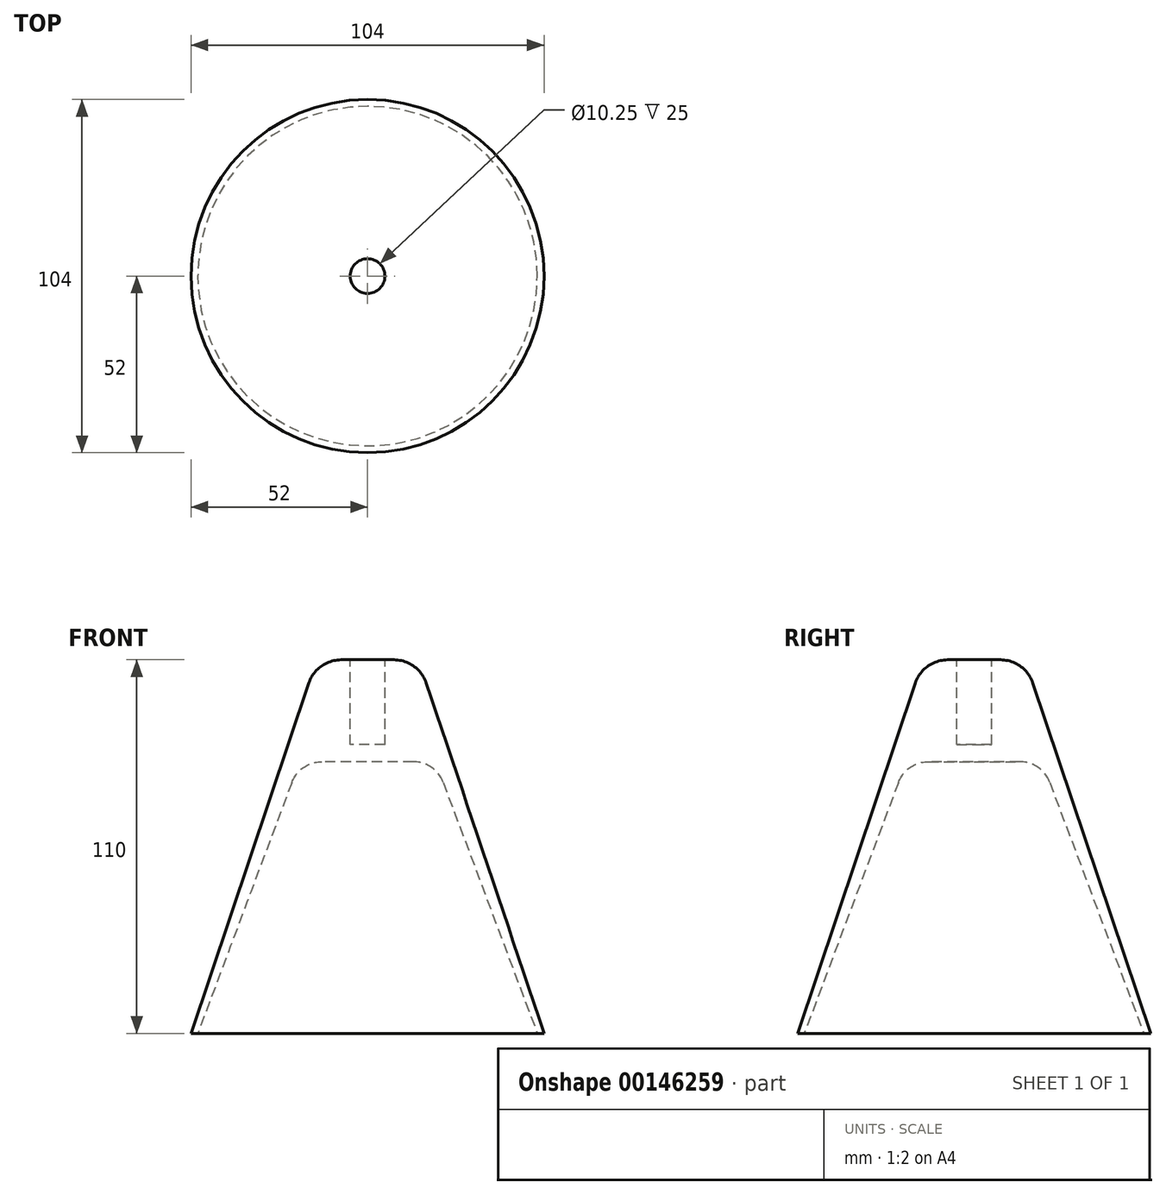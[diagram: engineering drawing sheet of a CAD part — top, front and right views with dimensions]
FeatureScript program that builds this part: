
annotation { "Feature Type Name" : "Feature", "Feature Type Description" : "" }
export const myFeature = defineFeature(function(context is Context, id is Id, definition is map)
    precondition{}
    {
        {
            var Q0;
            Q0=qCreatedBy(makeId("Top.planeOp"),FACE);
            var sketch = newSketch(context, id + "F0", { "sketchPlane" : qUnion([Q0])});
            skCircle(sketch, "E0", {"center": v(0, 0) * mm, "radius": 52 * mm});
            skSolve(sketch);
        }
        {
            var Q0;
            Q0=qCreatedBy(makeId("Top.planeOp"),FACE);
            cPlane(context, id + "F1", {"entities" : qUnion([Q0]), "cplaneType" : CPlaneType.OFFSET, "offset" : 80 * mm, "width" : 150 * mm, "height" : 150 * mm});
        }
        {
            var Q0;
            Q0=qCreatedBy(id+"F1.planeOp",FACE);
            var sketch = newSketch(context, id + "F2", { "sketchPlane" : qUnion([Q0])});
            skCircle(sketch, "E1", {"center": v(0, 0) * mm, "radius": 20 * mm});
            skSolve(sketch);
        }
        {
            var Q0;
            Q0=qCreatedBy(id+"F1.planeOp",FACE);
            cPlane(context, id + "F3", {"entities" : qUnion([Q0]), "cplaneType" : CPlaneType.OFFSET, "offset" : 30 * mm, "width" : 150 * mm, "height" : 150 * mm});
        }
        {
            var Q0;
            Q0=qCreatedBy(id+"F3.planeOp",FACE);
            var sketch = newSketch(context, id + "F4", { "sketchPlane" : qUnion([Q0])});
            skCircle(sketch, "E2", {"center": v(0, 0) * mm, "radius": 15 * mm});
            skSolve(sketch);
        }
        {
            var Q0;
            Q0=makeQuery(id+"F0.imprint","IMPRINT",FACE,{"disambiguationData":[TD([[makeQuery(id+"F0.imprint","IMPRINT",EDGE,{"derivedFrom":sQuery(id+"F0.wireOp",EDGE,"E0")}),1.0]])]});
            var Q1;
            Q1=makeQuery(id+"F4.imprint","IMPRINT",FACE,{"disambiguationData":[TD([[makeQuery(id+"F4.imprint","IMPRINT",EDGE,{"derivedFrom":sQuery(id+"F4.wireOp",EDGE,"E2")}),1.0]])]});
            loft(context, id + "F5", {"sheetProfilesArray" : [{ "sheetProfileEntities" : qUnion([Q0]) }, { "sheetProfileEntities" : qUnion([Q1]) }]});
        }
        {
            var Q0;
            Q0=makeQuery(id+"F5.opLoft","CAP_FACE",FACE,{"disambiguationData":[OSD([makeQuery(id+"F0.imprint","IMPRINT",FACE,{"disambiguationData":[TD([[makeQuery(id+"F0.imprint","IMPRINT",EDGE,{"derivedFrom":sQuery(id+"F0.wireOp",EDGE,"E0")}),1.0]])]})])],"isStart":true});
            var sketch = newSketch(context, id + "F6", { "sketchPlane" : qUnion([Q0])});
            skCircle(sketch, "E3", {"center": v(0, 0) * mm, "radius": 50 * mm});
            skSolve(sketch);
        }
        {
            var Q1;
            Q1 = qSketchRegion(id + "F2", true);
            var Q2;
            Q2 = qSketchRegion(id + "F6", true);
            loft(context, id + "F7", {"operationType" : NewBodyOperationType.REMOVE, "sheetProfilesArray" : [{ "sheetProfileEntities" : qUnion([Q1]) }, { "sheetProfileEntities" : qUnion([Q2]) }]});
        }
        {
            var Q0;
            Q0=makeQuery(id+"F5.opLoft","CAP_FACE",FACE,{"disambiguationData":[OSD([makeQuery(id+"F4.imprint","IMPRINT",FACE,{"disambiguationData":[TD([[makeQuery(id+"F4.imprint","IMPRINT",EDGE,{"derivedFrom":sQuery(id+"F4.wireOp",EDGE,"E2")}),1.0]])]})])],"isStart":true});
            var sketch = newSketch(context, id + "F8", { "sketchPlane" : qUnion([Q0])});
            skSolve(sketch);
        }
        {
            var Q0;
            Q0=makeQuery(id+"F8.imprint","IMPRINT",FACE,{"disambiguationData":[TD([[makeQuery(id+"F8.imprint","IMPRINT",EDGE,{"derivedFrom":makeQuery(id+"F5.opLoft","MID_CAP_EDGE",EDGE,{"disambiguationData":[OSD([sQuery(id+"F0.wireOp",EDGE,"E0"),sQuery(id+"F4.wireOp",EDGE,"E2")])],"capPos":1.0})}),1.0]])]});
            var sketch = newSketch(context, id + "F9", { "sketchPlane" : qUnion([Q0])});
            skCircle(sketch, "E4", {"center": v(0, 0) * mm, "radius": 5.12 * mm});
            skSolve(sketch);
        }
        {
            var Q0;
            Q0 = qSketchRegion(id + "F9", true);
            extrude(context, id + "F10", {"entities" : qUnion([Q0]), "operationType" : NewBodyOperationType.REMOVE, "oppositeDirection" : true, "depth" : 25 * mm});
        }
        {
            var Q0;
            Q0=makeQuery(id+"F5.opLoft","MID_CAP_EDGE",EDGE,{"disambiguationData":[OSD([sQuery(id+"F0.wireOp",EDGE,"E0"),sQuery(id+"F4.wireOp",EDGE,"E2")])],"capPos":1.0});
            fillet(context, id + "F11", {"entities" : qUnion([Q0]), "radius" : 10 * mm, "tangentPropagation" : true, "allowEdgeOverflow" : false});
        }
        {
            var Q0;
            Q0=makeQuery(id+"F7.boolean.opBoolean","COPY",EDGE,{"derivedFrom":makeQuery(id+"F7.opLoft","MID_CAP_EDGE",EDGE,{"disambiguationData":[OSD([sQuery(id+"F2.wireOp",EDGE,"E1")])],"capPos":0.0})});
            fillet(context, id + "F12", {"entities" : qUnion([Q0]), "radius" : 9.4 * mm, "tangentPropagation" : true, "allowEdgeOverflow" : false});
        }
    });
